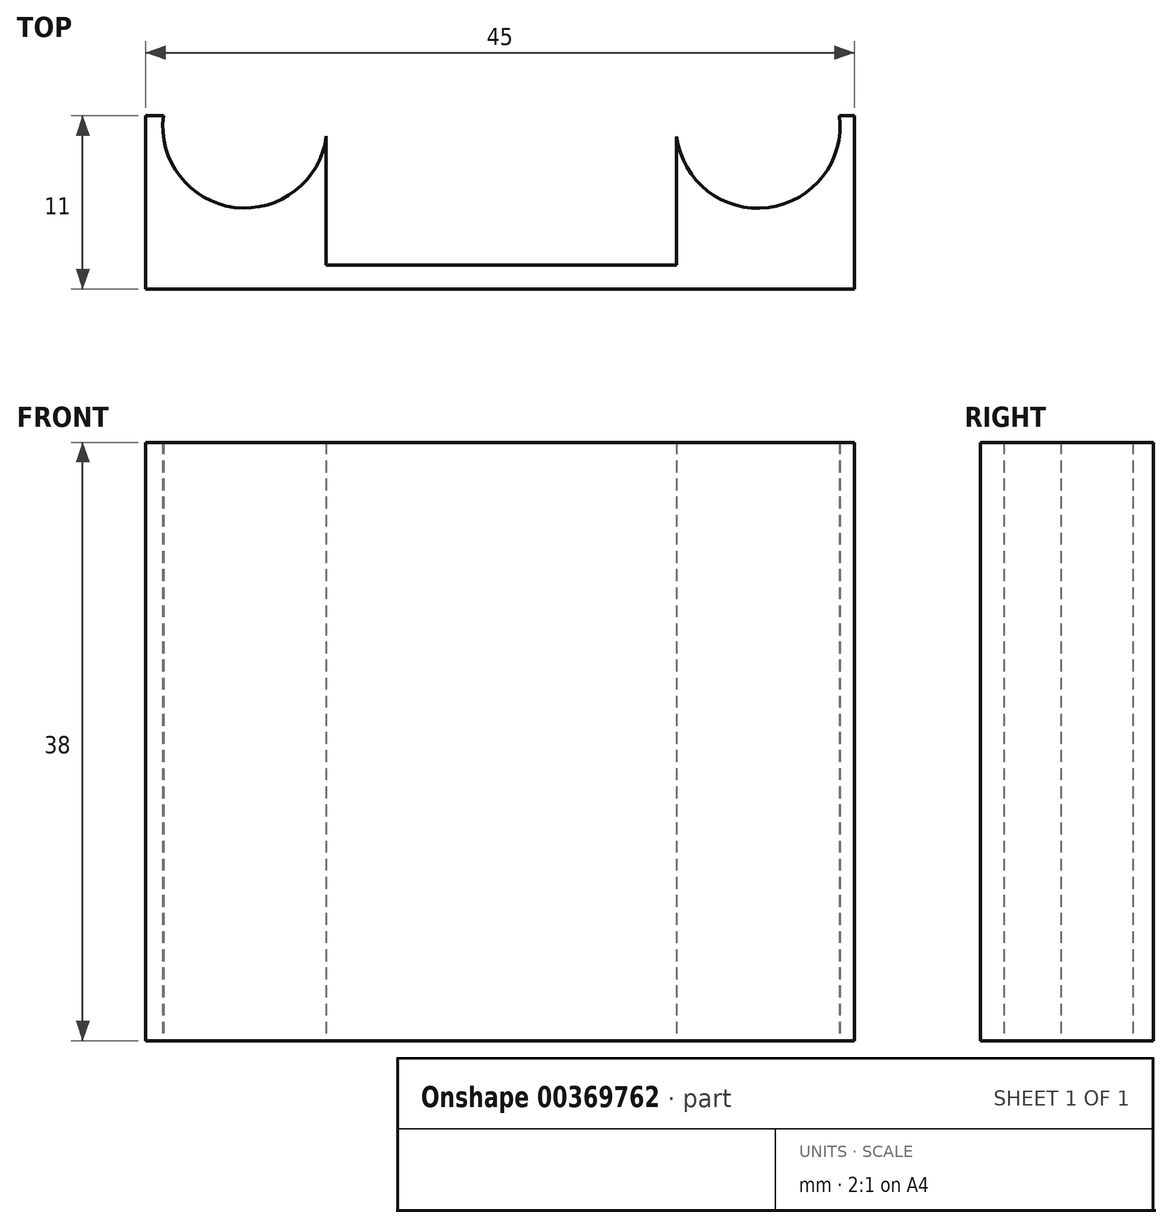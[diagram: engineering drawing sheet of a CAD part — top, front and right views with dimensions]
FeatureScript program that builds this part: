
annotation { "Feature Type Name" : "Feature", "Feature Type Description" : "" }
export const myFeature = defineFeature(function(context is Context, id is Id, definition is map)
    precondition{}
    {
        {
            var Q0;
            Q0=qCreatedBy(makeId("Top.planeOp"),FACE);
            var sketch = newSketch(context, id + "F0", { "sketchPlane" : qUnion([Q0])});
            skLineSegment(sketch, "E0.bottom", {"start": v(22.5, -5.5) * mm, "end": v(-22.5, -5.5) * mm});
            skLineSegment(sketch, "E0.top", {"start": v(22.5, 5.5) * mm, "end": v(-22.5, 5.5) * mm});
            skLineSegment(sketch, "E0.left", {"start": v(22.5, -5.5) * mm, "end": v(22.5, 5.5) * mm});
            skLineSegment(sketch, "E0.right", {"start": v(-22.5, -5.5) * mm, "end": v(-22.5, 5.5) * mm});
            skPoint(sketch, "E0.middle", {"position": v(0, 0) * mm});
            skSolve(sketch);
        }
        {
            var Q0;
            Q0=makeQuery(id+"F0.imprint","IMPRINT",FACE,{"disambiguationData":[TD([[makeQuery(id+"F0.imprint","IMPRINT",EDGE,{"derivedFrom":sQuery(id+"F0.wireOp",EDGE,"E0.bottom")}),-1.0]])]});
            var sketch = newSketch(context, id + "F1", { "sketchPlane" : qUnion([Q0])});
            skCircle(sketch, "E1", {"center": v(-16.2, 4.85) * mm, "radius": 5.22 * mm});
            skCircle(sketch, "E2", {"center": v(16.39, 4.84) * mm, "radius": 5.22 * mm});
            skSolve(sketch);
        }
        {
            var Q0;
            Q0=makeQuery(id+"F1.imprint","IMPRINT",FACE,{"disambiguationData":[TD([[makeQuery(id+"F1.imprint","IMPRINT",EDGE,{"derivedFrom":makeQuery(id+"F0.imprint","IMPRINT",EDGE,{"derivedFrom":sQuery(id+"F0.wireOp",EDGE,"E0.bottom")})}),-1.0]])]});
            extrude(context, id + "F2", {"entities" : qUnion([Q0]), "depth" : 38 * mm});
        }
        {
            var Q0;
            {var subQ0=sQuery(id+"F0.wireOp",EDGE,"E0.top");var subQ1=makeQuery(id+"F0.imprint","IMPRINT",EDGE,{"derivedFrom":subQ0});Q0=makeQuery(id+"F2.opExtrude","SWEPT_FACE",FACE,{"disambiguationData":[OSD([subQ0]),TDD([makeQuery(id+"F1.imprint","IMPRINT",EDGE,{"disambiguationData":[TD([[makeQuery(id+"F1.imprint","INTERSECT",VERTEX,{"disambiguationData":[OD(1.0)],"derivedFrom":[subQ1,sQuery(id+"F1.wireOp",EDGE,"E1")]}),1.0]])],"derivedFrom":subQ1})])]});}
            extrude(context, id + "F3", {"entities" : qUnion([Q0]), "operationType" : NewBodyOperationType.REMOVE, "oppositeDirection" : true, "depth" : 9.5 * mm});
        }
    });
